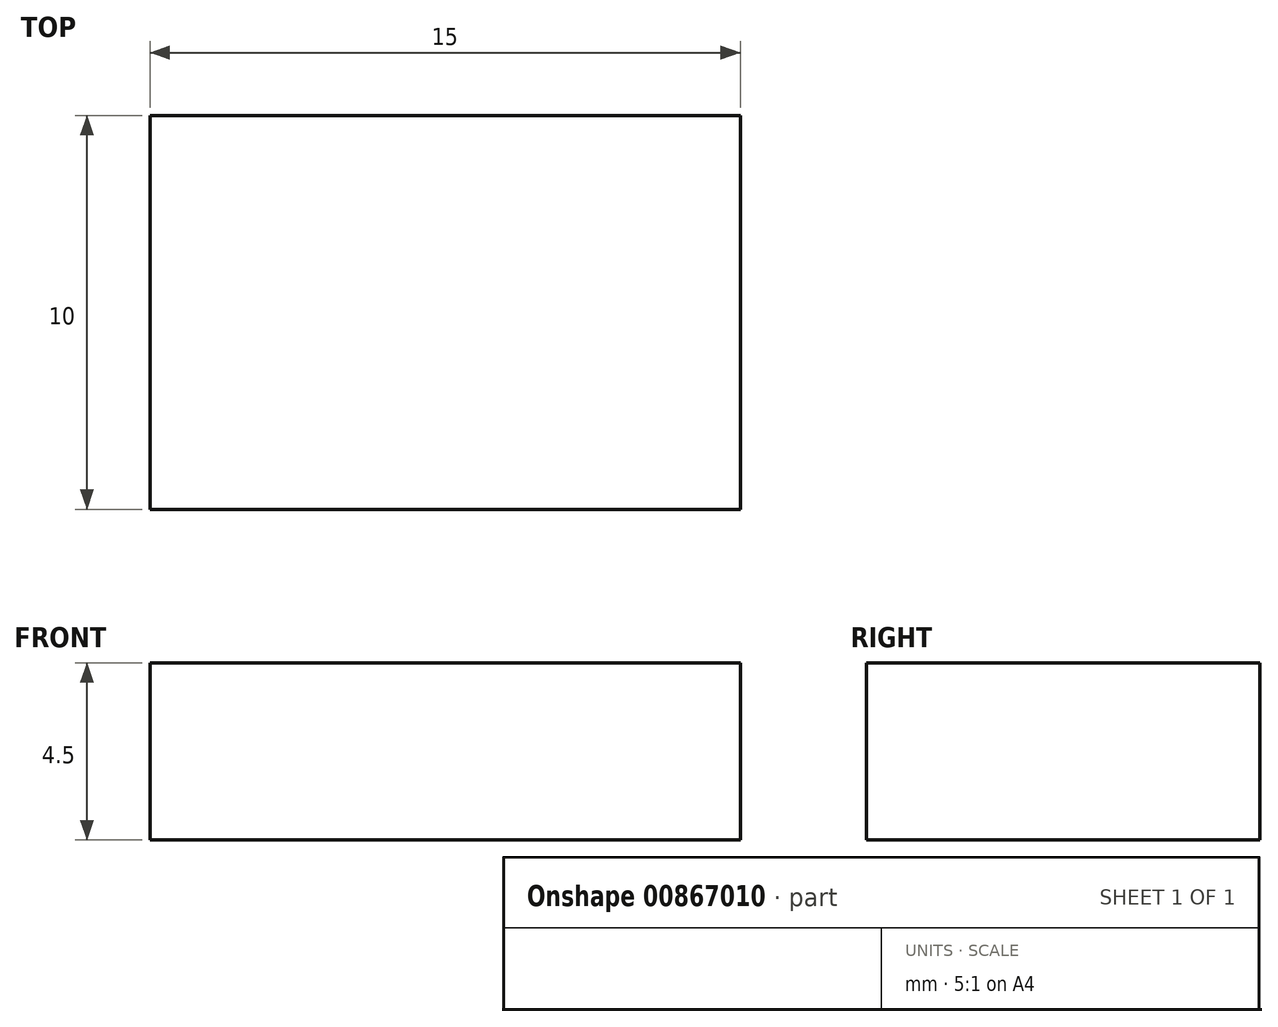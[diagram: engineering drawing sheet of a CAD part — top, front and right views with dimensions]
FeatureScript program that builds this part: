
annotation { "Feature Type Name" : "Feature", "Feature Type Description" : "" }
export const myFeature = defineFeature(function(context is Context, id is Id, definition is map)
    precondition{}
    {
        {
            var Q0;
            Q0=qCreatedBy(makeId("Top.planeOp"),FACE);
            var sketch = newSketch(context, id + "F0", { "sketchPlane" : qUnion([Q0])});
            skLineSegment(sketch, "E0.bottom", {"start": v(-7.5, 5) * mm, "end": v(7.5, 5) * mm});
            skLineSegment(sketch, "E0.top", {"start": v(-7.5, -5) * mm, "end": v(7.5, -5) * mm});
            skLineSegment(sketch, "E0.left", {"start": v(-7.5, 5) * mm, "end": v(-7.5, -5) * mm});
            skLineSegment(sketch, "E0.right", {"start": v(7.5, 5) * mm, "end": v(7.5, -5) * mm});
            skPoint(sketch, "E0.middle", {"position": v(0, 0) * mm});
            skSolve(sketch);
        }
        {
            var Q0;
            Q0 = qSketchRegion(id + "F0", true);
            extrude(context, id + "F1", {"entities" : qUnion([Q0]), "depth" : 4.5 * mm, "offsetDistance" : 25 * mm});
        }
    });
